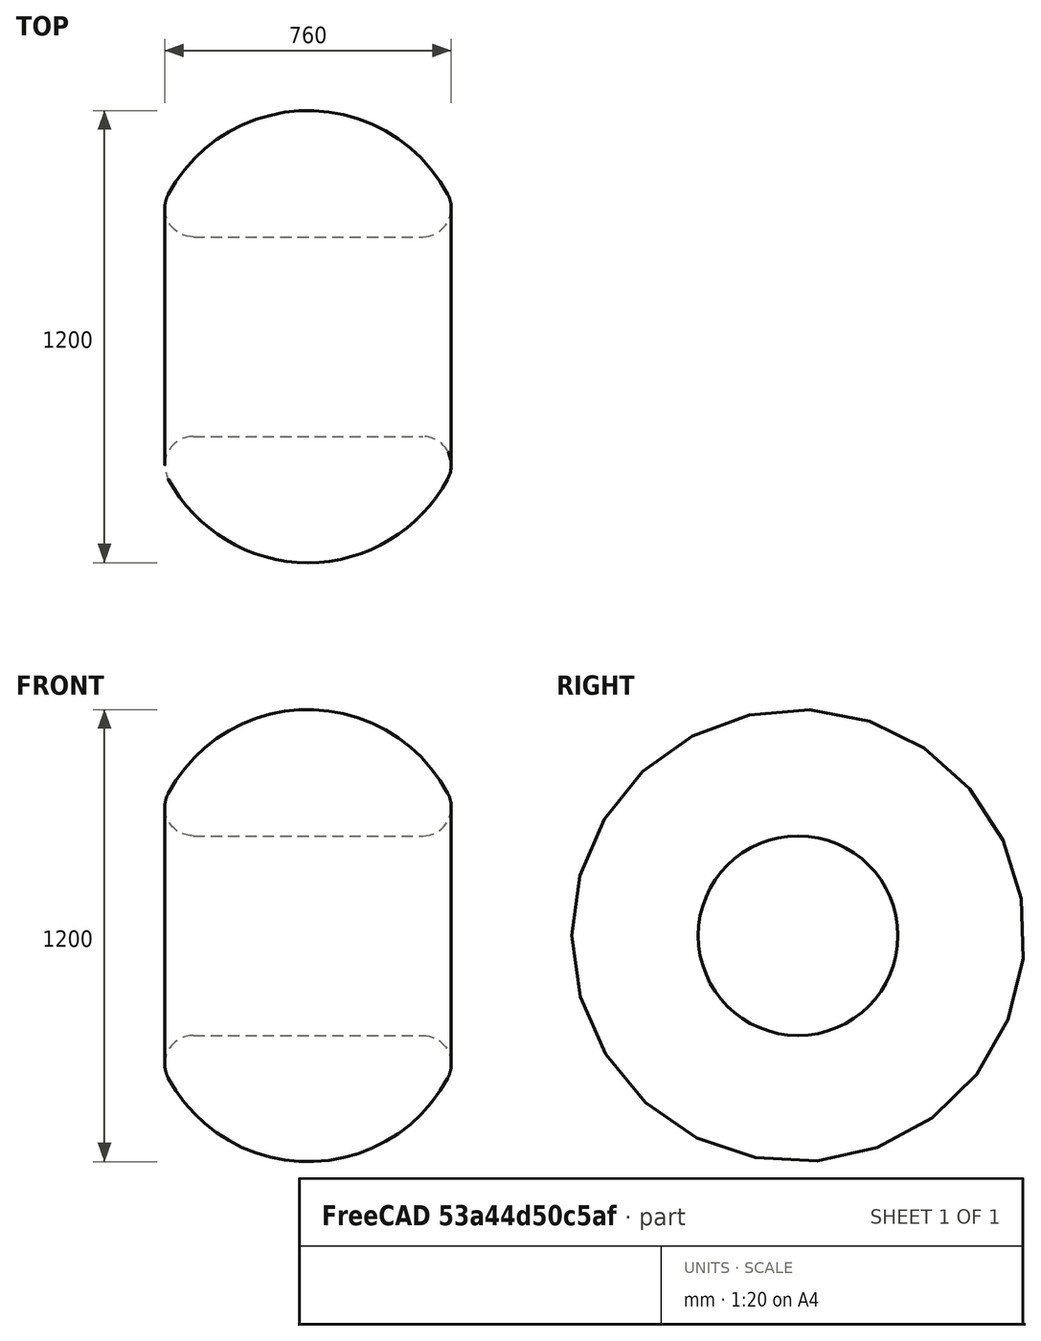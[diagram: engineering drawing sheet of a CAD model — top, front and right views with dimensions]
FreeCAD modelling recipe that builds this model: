
FCSTD DOCUMENT
Label: gyuru_HWR1R2
objects: Sketcher::SketchObject×1, PartDesign::Revolution×1
note: 2 computed .brp shape members not serialized (recipe doc carries the construction recipe); baked Part::Feature solids carry a one-line shape summary decoded from their .brp

FEATURE [Sketcher::SketchObject] Sketch001
  sketch-geometry (8):
    g0: LineSegment [constr] StartX=-370 StartY=-55.7012 StartZ=0 EndX=-370 EndY=-354.1 EndZ=0
    g1: LineSegment [constr] StartX=-219.417 StartY=-500 StartZ=0 EndX=385.318 EndY=-500 EndZ=0
    g2: ArcOfCircle CenterX=-294 CenterY=-258.609 CenterZ=0 NormalX=0 NormalY=0 NormalZ=1 Radius=76 StartAngle=1.5708 EndAngle=3.69042
    g3: ArcOfCircle CenterX=294 CenterY=-258.609 CenterZ=0 NormalX=0 NormalY=0 NormalZ=1 Radius=76 StartAngle=5.73435 EndAngle=7.85398
    g4: LineSegment StartX=-294 StartY=-182.609 StartZ=0 EndX=294 EndY=-182.609 EndZ=0
    g5: ArcOfCircle CenterX=0 CenterY=-80 CenterZ=0 NormalX=0 NormalY=0 NormalZ=1 Radius=420 StartAngle=3.69042 EndAngle=5.73435
    g6: LineSegment StartX=-358.838 StartY=-298.257 StartZ=0 EndX=-358.317 EndY=-299.11 EndZ=0
    g7: LineSegment StartX=358.317 StartY=-299.11 StartZ=0 EndX=358.838 EndY=-298.257 EndZ=0
  constraints (19):
    c: Vertical(g0)
    c: Horizontal(g1)
    c: DistanceY(g1) = -500
    c: DistanceX(g0) = -370
    c: Radius(g2) = 76
    c: Radius(g3) = 76
    c: Horizontal(g4)
    c: Tangent(g2,g4)
    c: Tangent(g4,g3)
    c: Radius(g5) = 420
    c: Tangent(g2,g6)
    c: Tangent(g6,g5)
    c: Tangent(g5,g7)
    c: Tangent(g7,g3)
    c: Distance(g6) = 1
    c: Distance(g7) = 1
    c: Tangent(g2,g0)
    c: Tangent(g5,g1)
    c: DistanceX(g5) = 0
FEATURE [PartDesign::Revolution] Revolution
  Angle = 360
  Axis = (1,0,0)
  Base = (0,0,0)
  Sketch = -> Sketch001
